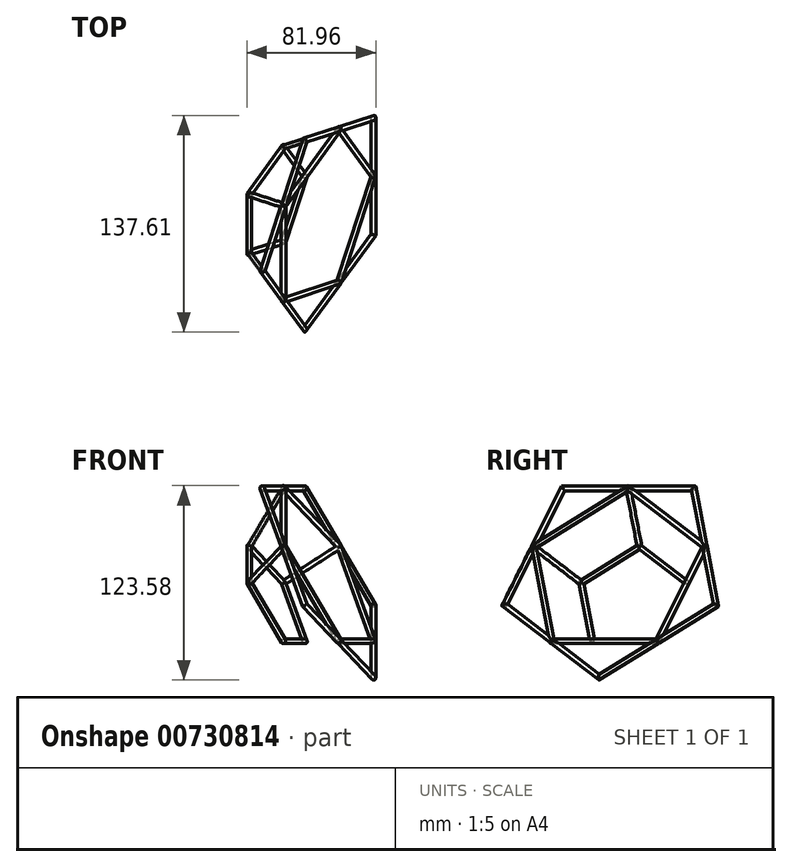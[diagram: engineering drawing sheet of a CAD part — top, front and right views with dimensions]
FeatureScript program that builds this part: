
annotation { "Feature Type Name" : "Feature", "Feature Type Description" : "" }
export const myFeature = defineFeature(function(context is Context, id is Id, definition is map)
    precondition{}
    {
        {
            var Q0;
            Q0=qCreatedBy(makeId("Top.planeOp"),FACE);
            var sketch = newSketch(context, id + "F0", { "sketchPlane" : qUnion([Q0])});
            skCircle(sketch, "E0.cCircle", {"center": v(0, 0) * mm, "radius": 30 * mm, "construction": true});
            skLineSegment(sketch, "E0.0", {"start": v(-21.8, 30) * mm, "end": v(21.8, 30) * mm});
            skLineSegment(sketch, "E0.1", {"start": v(21.8, 30) * mm, "end": v(35.27, -11.46) * mm, "construction": true});
            skLineSegment(sketch, "E0.2", {"start": v(35.27, -11.46) * mm, "end": v(0, -37.08) * mm, "construction": true});
            skLineSegment(sketch, "E0.3", {"start": v(0, -37.08) * mm, "end": v(-35.27, -11.46) * mm});
            skLineSegment(sketch, "E0.4", {"start": v(-35.27, -11.46) * mm, "end": v(-21.8, 30) * mm});
            skPoint(sketch, "E0.0.midPoint", {"position": v(0, 30) * mm});
            skLineSegment(sketch, "E1", {"start": v(0, -37.08) * mm, "end": v(21.8, 30) * mm});
            skSolve(sketch);
        }
        {
            var Q0;
            Q0=sQuery(id+"F0.wireOp",EDGE,"E0.4");
            cPlane(context, id + "F1", {"entities" : qUnion([Q0]), "cplaneType" : CPlaneType.LINE_ANGLE, "offset" : 25 * mm, "angle" : 63.44 * degree, "width" : 150 * mm, "height" : 150 * mm});
        }
        {
            var Q0;
            Q0=qCreatedBy(id+"F1.planeOp",FACE);
            var sketch = newSketch(context, id + "F2", { "sketchPlane" : qUnion([Q0])});
            skCircle(sketch, "E2.cCircle", {"center": v(6.24, 42.96) * mm, "radius": 30 * mm, "construction": true});
            skLineSegment(sketch, "E2.0", {"start": v(23.5, 10.14) * mm, "end": v(-19.64, 16.4) * mm});
            skLineSegment(sketch, "E2.1", {"start": v(-19.64, 16.4) * mm, "end": v(-27.01, 59.37) * mm});
            skLineSegment(sketch, "E2.2", {"start": v(-27.01, 59.37) * mm, "end": v(11.57, 79.66) * mm});
            skLineSegment(sketch, "E2.3", {"start": v(11.57, 79.66) * mm, "end": v(42.79, 49.23) * mm});
            skLineSegment(sketch, "E2.4", {"start": v(42.79, 49.23) * mm, "end": v(23.5, 10.14) * mm});
            skPoint(sketch, "E2.0.midPoint", {"position": v(1.93, 13.27) * mm});
            skCircle(sketch, "E3", {"center": v(42.79, 49.23) * mm, "radius": 1.5 * mm});
            skCircle(sketch, "E4.1.0", {"center": v(11.57, 79.66) * mm, "radius": 1.5 * mm});
            skCircle(sketch, "E4.2.0", {"center": v(-27.01, 59.37) * mm, "radius": 1.5 * mm});
            skCircle(sketch, "E4.3.0", {"center": v(-19.64, 16.4) * mm, "radius": 1.5 * mm});
            skCircle(sketch, "E4.4.0", {"center": v(23.5, 10.14) * mm, "radius": 1.5 * mm});
            skSolve(sketch);
        }
        {
            var Q0;
            Q0=sQuery(id+"F0.wireOp",VERTEX,"E0.3.start");
            var Q1;
            Q1=sQuery(id+"F0.wireOp",VERTEX,"E0.4.start");
            var Q2;
            Q2=sQuery(id+"F2.wireOp",VERTEX,"E2.2.start");
            cPlane(context, id + "F3", {"entities" : qUnion([Q0, Q1, Q2]), "cplaneType" : CPlaneType.THREE_POINT, "offset" : 25 * mm, "width" : 150 * mm, "height" : 150 * mm});
        }
        {
            var Q0;
            Q0=qCreatedBy(id+"F3.planeOp",FACE);
            var sketch = newSketch(context, id + "F4", { "sketchPlane" : qUnion([Q0])});
            skCircle(sketch, "E5.cCircle", {"center": v(-13.41, 41.29) * mm, "radius": 30 * mm, "construction": true});
            skLineSegment(sketch, "E5.0", {"start": v(-24.87, 6.02) * mm, "end": v(-50.5, 41.3) * mm});
            skLineSegment(sketch, "E5.1", {"start": v(-50.5, 41.3) * mm, "end": v(-24.87, 76.56) * mm});
            skLineSegment(sketch, "E5.2", {"start": v(-24.87, 76.56) * mm, "end": v(16.59, 63.08) * mm, "construction": true});
            skLineSegment(sketch, "E5.3", {"start": v(16.59, 63.08) * mm, "end": v(16.59, 19.5) * mm, "construction": true});
            skLineSegment(sketch, "E5.4", {"start": v(16.59, 19.5) * mm, "end": v(-24.87, 6.02) * mm});
            skPoint(sketch, "E5.0.midPoint", {"position": v(-37.68, 23.66) * mm});
            skLineSegment(sketch, "E6", {"start": v(-24.87, 76.56) * mm, "end": v(16.59, 19.5) * mm});
            skSolve(sketch);
        }
        {
            var Q0;
            Q0=sQuery(id+"F2.wireOp",VERTEX,"E2.4.start");
            var Q1;
            Q1=sQuery(id+"F0.wireOp",VERTEX,"E0.4.end");
            var Q2;
            Q2=sQuery(id+"F0.wireOp",VERTEX,"E0.1.start");
            cPlane(context, id + "F5", {"entities" : qUnion([Q0, Q1, Q2]), "cplaneType" : CPlaneType.THREE_POINT, "offset" : 25 * mm, "width" : 150 * mm, "height" : 150 * mm});
        }
        {
            var Q0;
            Q0=qCreatedBy(id+"F5.planeOp",FACE);
            var sketch = newSketch(context, id + "F6", { "sketchPlane" : qUnion([Q0])});
            skCircle(sketch, "E7.cCircle", {"center": v(0, 43.41) * mm, "radius": 30 * mm, "construction": true});
            skLineSegment(sketch, "E7.0", {"start": v(-35.27, 54.87) * mm, "end": v(0, 80.5) * mm, "construction": true});
            skLineSegment(sketch, "E7.1", {"start": v(0, 80.5) * mm, "end": v(35.26, 54.88) * mm});
            skLineSegment(sketch, "E7.2", {"start": v(35.26, 54.88) * mm, "end": v(21.8, 13.42) * mm});
            skLineSegment(sketch, "E7.3", {"start": v(21.8, 13.42) * mm, "end": v(-21.8, 13.41) * mm});
            skLineSegment(sketch, "E7.4", {"start": v(-21.8, 13.41) * mm, "end": v(-35.27, 54.87) * mm, "construction": true});
            skPoint(sketch, "E7.0.midPoint", {"position": v(-17.64, 67.68) * mm});
            skLineSegment(sketch, "E8", {"start": v(-21.8, 13.41) * mm, "end": v(0, 80.5) * mm});
            skSolve(sketch);
        }
        {
            var Q0;
            Q0=sQuery(id+"F6.wireOp",VERTEX,"E7.1.start");
            var Q1;
            Q1=sQuery(id+"F6.wireOp",VERTEX,"E7.2.start");
            var Q2;
            Q2=sQuery(id+"F2.wireOp",VERTEX,"E2.2.end");
            cPlane(context, id + "F7", {"entities" : qUnion([Q0, Q1, Q2]), "cplaneType" : CPlaneType.THREE_POINT, "offset" : 25 * mm, "width" : 150 * mm, "height" : 150 * mm});
        }
        {
            var Q0;
            Q0=qCreatedBy(id+"F7.planeOp",FACE);
            var sketch = newSketch(context, id + "F8", { "sketchPlane" : qUnion([Q0])});
            skCircle(sketch, "E9.cCircle", {"center": v(13.42, 41.29) * mm, "radius": 30 * mm, "construction": true});
            skLineSegment(sketch, "E9.0", {"start": v(1.96, 76.56) * mm, "end": v(43.42, 63.08) * mm, "construction": true});
            skLineSegment(sketch, "E9.1", {"start": v(43.42, 63.08) * mm, "end": v(43.42, 19.49) * mm, "construction": true});
            skLineSegment(sketch, "E9.2", {"start": v(43.42, 19.49) * mm, "end": v(1.96, 6.02) * mm});
            skLineSegment(sketch, "E9.3", {"start": v(1.96, 6.02) * mm, "end": v(-23.66, 41.29) * mm});
            skLineSegment(sketch, "E9.4", {"start": v(-23.66, 41.29) * mm, "end": v(1.96, 76.56) * mm});
            skPoint(sketch, "E9.0.midPoint", {"position": v(22.69, 69.82) * mm});
            skLineSegment(sketch, "E10", {"start": v(43.42, 19.49) * mm, "end": v(1.96, 76.56) * mm});
            skSolve(sketch);
        }
        {
            var Q0;
            Q0=sQuery(id+"F8.wireOp",VERTEX,"E9.4.start");
            var Q1;
            Q1=sQuery(id+"F8.wireOp",VERTEX,"E9.0.start");
            var Q2;
            Q2=sQuery(id+"F4.wireOp",VERTEX,"E5.2.start");
            cPlane(context, id + "F9", {"entities" : qUnion([Q0, Q1, Q2]), "cplaneType" : CPlaneType.THREE_POINT, "offset" : 25 * mm, "width" : 150 * mm, "height" : 150 * mm});
        }
        {
            var Q0;
            Q0=qCreatedBy(id+"F9.planeOp",FACE);
            var sketch = newSketch(context, id + "F10", { "sketchPlane" : qUnion([Q0])});
            skCircle(sketch, "E11.cCircle", {"center": v(-6.24, 42.96) * mm, "radius": 30 * mm, "construction": true});
            skLineSegment(sketch, "E11.0", {"start": v(-39.5, 26.55) * mm, "end": v(-32.12, 69.52) * mm});
            skLineSegment(sketch, "E11.1", {"start": v(-32.12, 69.52) * mm, "end": v(11.02, 75.78) * mm, "construction": true});
            skLineSegment(sketch, "E11.2", {"start": v(11.02, 75.78) * mm, "end": v(30.3, 36.7) * mm, "construction": true});
            skLineSegment(sketch, "E11.3", {"start": v(30.3, 36.7) * mm, "end": v(-0.91, 6.27) * mm});
            skLineSegment(sketch, "E11.4", {"start": v(-0.91, 6.27) * mm, "end": v(-39.5, 26.55) * mm});
            skPoint(sketch, "E11.0.midPoint", {"position": v(-35.81, 48.04) * mm});
            skLineSegment(sketch, "E12", {"start": v(-32.12, 69.52) * mm, "end": v(30.3, 36.7) * mm});
            skSolve(sketch);
        }
        {
            var Q0;
            Q0=sQuery(id+"F4.wireOp",VERTEX,"E6.end");
            var Q1;
            Q1=sQuery(id+"F8.wireOp",VERTEX,"E10.start");
            var Q2;
            Q2=sQuery(id+"F10.wireOp",VERTEX,"E12.start");
            cPlane(context, id + "F11", {"entities" : qUnion([Q0, Q1, Q2]), "cplaneType" : CPlaneType.THREE_POINT, "offset" : 25 * mm, "width" : 150 * mm, "height" : 150 * mm});
        }
        {
            var Q0;
            Q0=qCreatedBy(id+"F11.planeOp",FACE);
            var sketch = newSketch(context, id + "F12", { "sketchPlane" : qUnion([Q0])});
            skLineSegment(sketch, "E13", {"start": v(-34.16, -10.14) * mm, "end": v(-72.75, 10.14) * mm});
            skLineSegment(sketch, "E14", {"start": v(-72.75, 10.14) * mm, "end": v(-65.38, 53.1) * mm});
            skLineSegment(sketch, "E15", {"start": v(-72.75, 10.14) * mm, "end": v(-49.77, 21.48) * mm, "construction": true});
            skLineSegment(sketch, "E16.1.0", {"start": v(35.64, 0) * mm, "end": v(4.42, -30.43) * mm});
            skLineSegment(sketch, "E16.1.1", {"start": v(4.42, -30.43) * mm, "end": v(-34.16, -10.14) * mm});
            skLineSegment(sketch, "E16.2.0", {"start": v(47.56, 69.52) * mm, "end": v(66.85, 30.43) * mm});
            skLineSegment(sketch, "E16.2.1", {"start": v(66.85, 30.43) * mm, "end": v(35.64, 0) * mm});
            skLineSegment(sketch, "E16.3.0", {"start": v(-14.87, 102.34) * mm, "end": v(28.27, 108.6) * mm});
            skLineSegment(sketch, "E16.3.1", {"start": v(28.27, 108.6) * mm, "end": v(47.56, 69.52) * mm});
            skLineSegment(sketch, "E16.4.0", {"start": v(-65.38, 53.1) * mm, "end": v(-58, 96.07) * mm});
            skLineSegment(sketch, "E16.4.1", {"start": v(-58, 96.07) * mm, "end": v(-14.87, 102.34) * mm});
            skPoint(sketch, "E16.center", {"position": v(-6.24, 42.96) * mm});
            skLineSegment(sketch, "E17", {"start": v(-6.24, 42.96) * mm, "end": v(-58, 96.07) * mm, "construction": true});
            skLineSegment(sketch, "E18", {"start": v(-6.24, 42.96) * mm, "end": v(-72.75, 10.14) * mm, "construction": true});
            skLineSegment(sketch, "E19", {"start": v(-6.24, 42.96) * mm, "end": v(4.42, -30.43) * mm, "construction": true});
            skLineSegment(sketch, "E20", {"start": v(-6.24, 42.96) * mm, "end": v(66.85, 30.43) * mm, "construction": true});
            skLineSegment(sketch, "E21", {"start": v(-6.24, 42.96) * mm, "end": v(28.27, 108.6) * mm, "construction": true});
            skLineSegment(sketch, "E22", {"start": v(-14.87, 102.34) * mm, "end": v(-6.24, 42.96) * mm, "construction": true});
            skLineSegment(sketch, "E23", {"start": v(47.56, 69.52) * mm, "end": v(-6.24, 42.96) * mm, "construction": true});
            skLineSegment(sketch, "E24", {"start": v(35.64, 0) * mm, "end": v(-6.24, 42.96) * mm, "construction": true});
            skLineSegment(sketch, "E25", {"start": v(-34.16, -10.14) * mm, "end": v(-6.24, 42.96) * mm, "construction": true});
            skLineSegment(sketch, "E26", {"start": v(-6.24, 42.96) * mm, "end": v(-65.38, 53.1) * mm, "construction": true});
            skSolve(sketch);
        }
        {
            var Q0;
            Q0=sQuery(id+"F6.wireOp",EDGE,"E8");
            var Q1;
            Q1=sQuery(id+"F6.wireOp",VERTEX,"E7.cCircle.center");
            cPlane(context, id + "F13", {"entities" : qUnion([Q0, Q1]), "cplaneType" : CPlaneType.LINE_POINT, "offset" : 25 * mm, "oppositeDirection" : true, "width" : 150 * mm, "height" : 150 * mm});
        }
        {
            var Q0;
            Q0=qCreatedBy(id+"F13.planeOp",FACE);
            var sketch = newSketch(context, id + "F14", { "sketchPlane" : qUnion([Q0])});
            skCircle(sketch, "E27", {"center": v(24.87, 26.83) * mm, "radius": 1.5 * mm});
            skCircle(sketch, "E28", {"center": v(-16.59, 26.83) * mm, "radius": 1.5 * mm});
            skCircle(sketch, "E29", {"center": v(-23.66, -70.25) * mm, "radius": 1.5 * mm});
            skSolve(sketch);
        }
        {
            var Q0;
            Q0=makeQuery(id+"F14.imprint","IMPRINT",FACE,{"disambiguationData":[TD([[makeQuery(id+"F14.imprint","IMPRINT",EDGE,{"derivedFrom":sQuery(id+"F14.wireOp",EDGE,"E27")}),1.0]])]});
            var Q1;
            Q1=sQuery(id+"F6.wireOp",EDGE,"E8");
            var Q2;
            Q2=sQuery(id+"F0.wireOp",EDGE,"E1");
            var Q3;
            Q3=sQuery(id+"F4.wireOp",EDGE,"E6");
            var Q4;
            Q4=sQuery(id+"F10.wireOp",EDGE,"E12");
            var Q5;
            Q5=sQuery(id+"F8.wireOp",EDGE,"E10");
            sweep(context, id + "F15", {"profiles" : qUnion([Q0]), "path" : qUnion([Q1, Q2, Q3, Q4, Q5])});
        }
        {
            var Q0;
            Q0=makeQuery(id+"F14.imprint","IMPRINT",FACE,{"disambiguationData":[TD([[makeQuery(id+"F14.imprint","IMPRINT",EDGE,{"derivedFrom":sQuery(id+"F14.wireOp",EDGE,"E28")}),1.0]])]});
            var Q1;
            Q1=sQuery(id+"F14.wireOp",EDGE,"E28");
            var Q2;
            Q2=sQuery(id+"F2.wireOp",EDGE,"E2.4");
            var Q3;
            Q3=sQuery(id+"F2.wireOp",EDGE,"E2.3");
            var Q4;
            Q4=sQuery(id+"F2.wireOp",EDGE,"E2.2");
            var Q5;
            Q5=sQuery(id+"F2.wireOp",EDGE,"E2.1");
            var Q6;
            Q6=sQuery(id+"F2.wireOp",EDGE,"E2.0");
            sweep(context, id + "F16", {"profiles" : qUnion([Q0]), "surfaceProfiles" : qUnion([Q1]), "path" : qUnion([Q2, Q3, Q4, Q5, Q6])});
        }
        {
            var Q0;
            {var subQ0=sQuery(id+"F2.wireOp",EDGE,"E2.4");var subQ1=sQuery(id+"F2.wireOp",EDGE,"E2.3");var subQ2=makeQuery(id+"F2.imprint","INTERSECT",VERTEX,{"derivedFrom":[subQ1,subQ0]});Q0=makeQuery(id+"F2.imprint","IMPRINT",FACE,{"disambiguationData":[TD([[makeQuery(id+"F2.imprint","IMPRINT",EDGE,{"disambiguationData":[TD([[subQ2,1.0]])],"derivedFrom":subQ1}),-1.0]])]});}
            var Q1;
            {var subQ0=sQuery(id+"F2.wireOp",EDGE,"E2.4");var subQ1=sQuery(id+"F2.wireOp",EDGE,"E2.3");var subQ2=makeQuery(id+"F2.imprint","INTERSECT",VERTEX,{"derivedFrom":[subQ1,subQ0]});Q1=makeQuery(id+"F2.imprint","IMPRINT",FACE,{"disambiguationData":[TD([[makeQuery(id+"F2.imprint","IMPRINT",EDGE,{"disambiguationData":[TD([[subQ2,1.0]])],"derivedFrom":subQ1}),1.0]])]});}
            var Q2;
            Q2=sQuery(id+"F6.wireOp",EDGE,"E7.1");
            sweep(context, id + "F17", {"operationType" : NewBodyOperationType.ADD, "profiles" : qUnion([Q0, Q1]), "path" : qUnion([Q2])});
        }
        {
            var Q0;
            {var subQ0=sQuery(id+"F2.wireOp",EDGE,"E2.3");var subQ1=sQuery(id+"F2.wireOp",EDGE,"E2.2");var subQ2=makeQuery(id+"F2.imprint","INTERSECT",VERTEX,{"derivedFrom":[subQ1,subQ0]});Q0=makeQuery(id+"F2.imprint","IMPRINT",FACE,{"disambiguationData":[TD([[makeQuery(id+"F2.imprint","IMPRINT",EDGE,{"disambiguationData":[TD([[subQ2,1.0]])],"derivedFrom":subQ1}),-1.0]])]});}
            var Q1;
            {var subQ0=sQuery(id+"F2.wireOp",EDGE,"E2.3");var subQ1=sQuery(id+"F2.wireOp",EDGE,"E2.2");var subQ2=makeQuery(id+"F2.imprint","INTERSECT",VERTEX,{"derivedFrom":[subQ1,subQ0]});Q1=makeQuery(id+"F2.imprint","IMPRINT",FACE,{"disambiguationData":[TD([[makeQuery(id+"F2.imprint","IMPRINT",EDGE,{"disambiguationData":[TD([[subQ2,1.0]])],"derivedFrom":subQ1}),1.0]])]});}
            var Q2;
            Q2=sQuery(id+"F8.wireOp",EDGE,"E9.4");
            sweep(context, id + "F18", {"operationType" : NewBodyOperationType.ADD, "profiles" : qUnion([Q0, Q1]), "path" : qUnion([Q2])});
        }
        {
            var Q0;
            {var subQ0=sQuery(id+"F2.wireOp",EDGE,"E2.2");var subQ1=sQuery(id+"F2.wireOp",EDGE,"E2.1");var subQ2=makeQuery(id+"F2.imprint","INTERSECT",VERTEX,{"derivedFrom":[subQ1,subQ0]});Q0=makeQuery(id+"F2.imprint","IMPRINT",FACE,{"disambiguationData":[TD([[makeQuery(id+"F2.imprint","IMPRINT",EDGE,{"disambiguationData":[TD([[subQ2,1.0]])],"derivedFrom":subQ1}),-1.0]])]});}
            var Q1;
            {var subQ0=sQuery(id+"F2.wireOp",EDGE,"E2.2");var subQ1=sQuery(id+"F2.wireOp",EDGE,"E2.1");var subQ2=makeQuery(id+"F2.imprint","INTERSECT",VERTEX,{"derivedFrom":[subQ1,subQ0]});Q1=makeQuery(id+"F2.imprint","IMPRINT",FACE,{"disambiguationData":[TD([[makeQuery(id+"F2.imprint","IMPRINT",EDGE,{"disambiguationData":[TD([[subQ2,1.0]])],"derivedFrom":subQ1}),1.0]])]});}
            var Q2;
            Q2=sQuery(id+"F4.wireOp",EDGE,"E5.1");
            sweep(context, id + "F19", {"operationType" : NewBodyOperationType.ADD, "profiles" : qUnion([Q0, Q1]), "path" : qUnion([Q2])});
        }
        {
            var Q0;
            Q0=makeQuery(id+"F14.imprint","IMPRINT",FACE,{"disambiguationData":[TD([[makeQuery(id+"F14.imprint","IMPRINT",EDGE,{"derivedFrom":sQuery(id+"F14.wireOp",EDGE,"E29")}),1.0]])]});
            var Q1;
            Q1=sQuery(id+"F12.wireOp",EDGE,"E16.3.1");
            var Q2;
            Q2=sQuery(id+"F12.wireOp",EDGE,"E16.3.0");
            var Q3;
            Q3=sQuery(id+"F12.wireOp",EDGE,"E16.4.1");
            var Q4;
            Q4=sQuery(id+"F12.wireOp",EDGE,"E16.4.0");
            sweep(context, id + "F20", {"operationType" : NewBodyOperationType.ADD, "profiles" : qUnion([Q0]), "path" : qUnion([Q1, Q2, Q3, Q4])});
        }
        {
            var Q0;
            Q0=makeQuery(id+"F14.imprint","IMPRINT",FACE,{"disambiguationData":[TD([[makeQuery(id+"F14.imprint","IMPRINT",EDGE,{"derivedFrom":sQuery(id+"F14.wireOp",EDGE,"E29")}),1.0]])]});
            var Q1;
            Q1=sQuery(id+"F12.wireOp",EDGE,"E16.2.0");
            var Q2;
            Q2=sQuery(id+"F12.wireOp",EDGE,"E16.2.1");
            var Q3;
            Q3=sQuery(id+"F12.wireOp",EDGE,"E16.1.0");
            var Q4;
            Q4=sQuery(id+"F12.wireOp",EDGE,"E16.1.1");
            var Q5;
            Q5=sQuery(id+"F12.wireOp",EDGE,"E13");
            var Q6;
            Q6=sQuery(id+"F12.wireOp",EDGE,"E14");
            sweep(context, id + "F21", {"operationType" : NewBodyOperationType.ADD, "profiles" : qUnion([Q0]), "path" : qUnion([Q1, Q2, Q3, Q4, Q5, Q6])});
        }
    });
